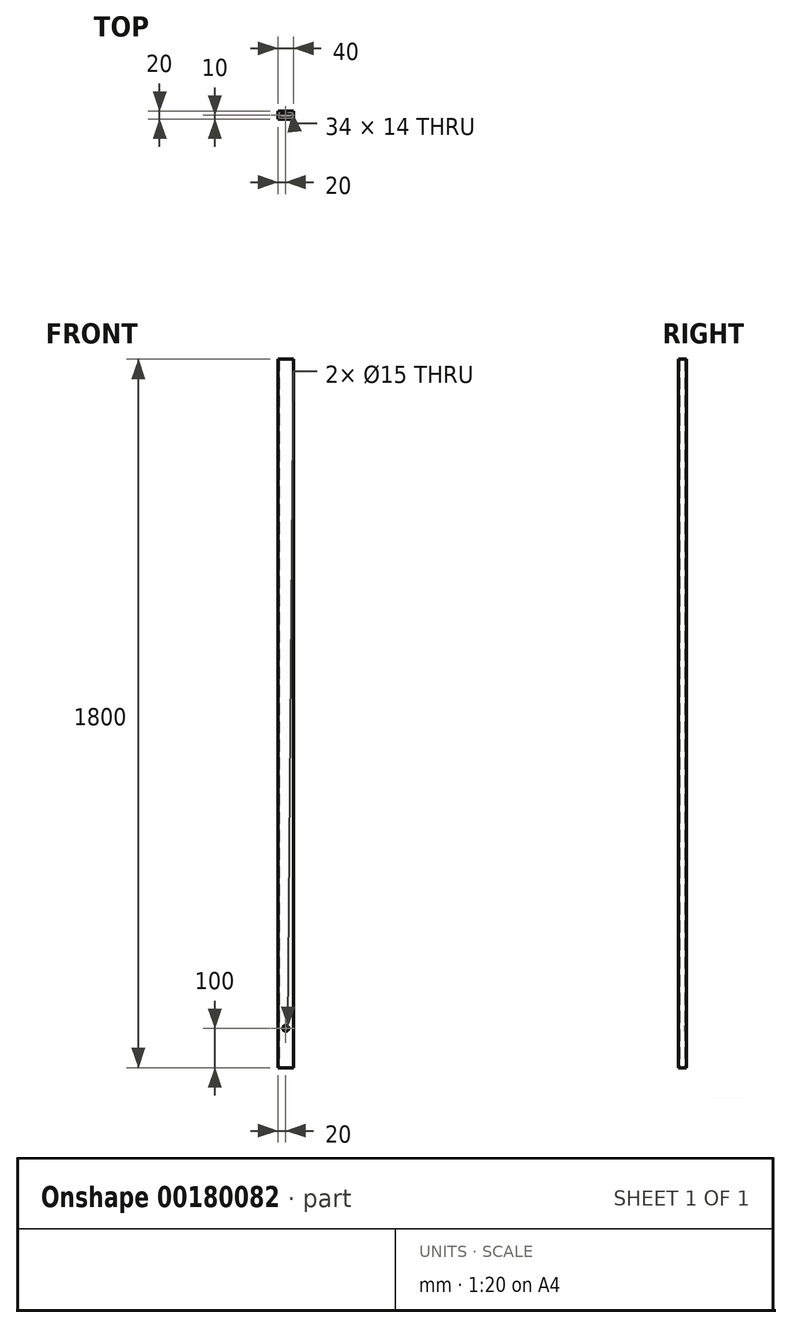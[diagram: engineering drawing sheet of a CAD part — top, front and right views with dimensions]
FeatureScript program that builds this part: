
annotation { "Feature Type Name" : "Feature", "Feature Type Description" : "" }
export const myFeature = defineFeature(function(context is Context, id is Id, definition is map)
    precondition{}
    {
        {
            var Q0;
            Q0=qCreatedBy(makeId("Top.planeOp"),FACE);
            var sketch = newSketch(context, id + "F0", { "sketchPlane" : qUnion([Q0])});
            skLineSegment(sketch, "E0.bottom", {"start": v(20, -10) * mm, "end": v(-20, -10) * mm});
            skLineSegment(sketch, "E0.top", {"start": v(20, 10) * mm, "end": v(-20, 10) * mm});
            skLineSegment(sketch, "E0.left", {"start": v(20, -10) * mm, "end": v(20, 10) * mm});
            skLineSegment(sketch, "E0.right", {"start": v(-20, -10) * mm, "end": v(-20, 10) * mm});
            skPoint(sketch, "E0.middle", {"position": v(0, 0) * mm});
            skLineSegment(sketch, "E1.0", {"start": v(17, 7) * mm, "end": v(-17, 7) * mm});
            skLineSegment(sketch, "E1.1", {"start": v(17, -7) * mm, "end": v(17, 7) * mm});
            skLineSegment(sketch, "E1.2", {"start": v(17, -7) * mm, "end": v(-17, -7) * mm});
            skLineSegment(sketch, "E1.3", {"start": v(-17, -7) * mm, "end": v(-17, 7) * mm});
            skSolve(sketch);
        }
        {
            var Q0;
            Q0=makeQuery(id+"F0.imprint","IMPRINT",FACE,{"disambiguationData":[TD([[makeQuery(id+"F0.imprint","IMPRINT",EDGE,{"derivedFrom":sQuery(id+"F0.wireOp",EDGE,"E0.bottom")}),-1.0]])]});
            extrude(context, id + "F1", {"entities" : qUnion([Q0]), "depth" : 1800 * mm});
        }
        {
            var Q0;
            Q0=makeQuery(id+"F1.opExtrude","SWEPT_FACE",FACE,{"disambiguationData":[OSD([sQuery(id+"F0.wireOp",EDGE,"E0.bottom")])]});
            var sketch = newSketch(context, id + "F2", { "sketchPlane" : qUnion([Q0])});
            skCircle(sketch, "E2", {"center": v(0, 100) * mm, "radius": 7.5 * mm});
            skSolve(sketch);
        }
        {
            var Q0;
            Q0=makeQuery(id+"F2.imprint","IMPRINT",FACE,{"disambiguationData":[TD([[makeQuery(id+"F2.imprint","IMPRINT",EDGE,{"derivedFrom":sQuery(id+"F2.wireOp",EDGE,"E2")}),1.0]])]});
            extrude(context, id + "F3", {"entities" : qUnion([Q0]), "operationType" : NewBodyOperationType.REMOVE, "oppositeDirection" : true, "depth" : 20 * mm});
        }
    });
